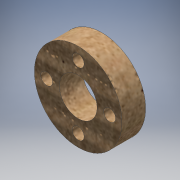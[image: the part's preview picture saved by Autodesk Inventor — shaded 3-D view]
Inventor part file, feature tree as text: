
AUTODESK INVENTOR PART (.ipt)
format: ipt  version: 2016 (Build 200138000, 138)  size: 153,088 bytes
history: native  units: mm
features: extrude x1, sketch x1
ambient origin geometry x8: Origin, YZ Plane, XZ Plane, XY Plane, X Axis, Y Axis, Z Axis, Center Point
bodies: Solid1 (feature_tree)
feature tree (2):
  extrude  "Extrusion1"  Depth=5.95mm
  sketch  "Sketch1"  dims[d0=22.098mm d1=3.0mm d2=7.9375mm d3=40.0mm d5=360.0deg d7=9.525mm d8=5.95mm d9=0.0mm]
